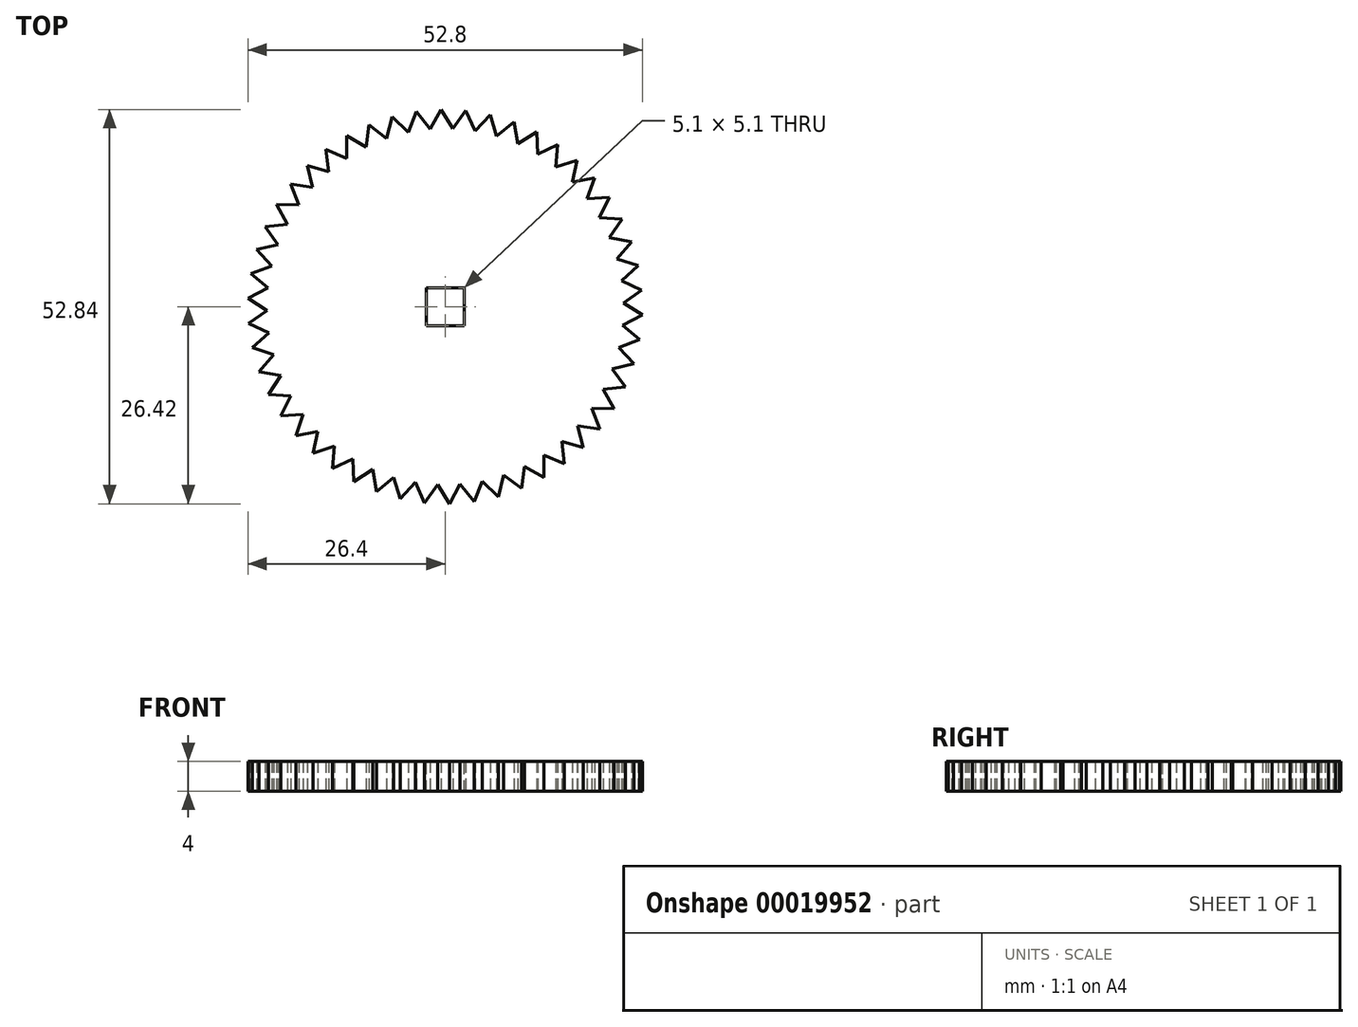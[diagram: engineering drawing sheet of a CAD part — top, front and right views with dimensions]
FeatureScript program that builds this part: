
annotation { "Feature Type Name" : "Feature", "Feature Type Description" : "" }
export const myFeature = defineFeature(function(context is Context, id is Id, definition is map)
    precondition{}
    {
        {
            var Q0;
            Q0=qCreatedBy(makeId("Top.planeOp"),FACE);
            var sketch = newSketch(context, id + "F0", { "sketchPlane" : qUnion([Q0])});
            skCircle(sketch, "E0.cCircle", {"center": v(0, 0) * mm, "radius": 23.83 * mm, "construction": true});
            skLineSegment(sketch, "E0.0", {"start": v(-2, 23.79) * mm, "end": v(1, 23.85) * mm});
            skLineSegment(sketch, "E0.1", {"start": v(1, 23.85) * mm, "end": v(3.98, 23.54) * mm});
            skLineSegment(sketch, "E0.2", {"start": v(3.98, 23.54) * mm, "end": v(6.9, 22.85) * mm});
            skLineSegment(sketch, "E0.3", {"start": v(6.9, 22.85) * mm, "end": v(9.71, 21.8) * mm});
            skLineSegment(sketch, "E0.4", {"start": v(9.71, 21.8) * mm, "end": v(12.37, 20.42) * mm});
            skLineSegment(sketch, "E0.5", {"start": v(12.37, 20.42) * mm, "end": v(14.83, 18.7) * mm});
            skLineSegment(sketch, "E0.6", {"start": v(14.83, 18.7) * mm, "end": v(17.06, 16.7) * mm});
            skLineSegment(sketch, "E0.7", {"start": v(17.06, 16.7) * mm, "end": v(19.02, 14.43) * mm});
            skLineSegment(sketch, "E0.8", {"start": v(19.02, 14.43) * mm, "end": v(20.67, 11.94) * mm});
            skLineSegment(sketch, "E0.9", {"start": v(20.67, 11.94) * mm, "end": v(22, 9.25) * mm});
            skLineSegment(sketch, "E0.10", {"start": v(22, 9.25) * mm, "end": v(23, 6.42) * mm});
            skLineSegment(sketch, "E0.11", {"start": v(23, 6.42) * mm, "end": v(23.62, 3.49) * mm});
            skLineSegment(sketch, "E0.12", {"start": v(23.62, 3.49) * mm, "end": v(23.87, 0.5) * mm});
            skLineSegment(sketch, "E0.13", {"start": v(23.87, 0.5) * mm, "end": v(23.74, -2.5) * mm});
            skLineSegment(sketch, "E0.14", {"start": v(23.74, -2.5) * mm, "end": v(23.24, -5.45) * mm});
            skLineSegment(sketch, "E0.15", {"start": v(23.24, -5.45) * mm, "end": v(22.38, -8.32) * mm});
            skLineSegment(sketch, "E0.16", {"start": v(22.38, -8.32) * mm, "end": v(21.16, -11.06) * mm});
            skLineSegment(sketch, "E0.17", {"start": v(21.16, -11.06) * mm, "end": v(19.6, -13.62) * mm});
            skLineSegment(sketch, "E0.18", {"start": v(19.6, -13.62) * mm, "end": v(17.74, -15.97) * mm});
            skLineSegment(sketch, "E0.19", {"start": v(17.74, -15.97) * mm, "end": v(15.6, -18.07) * mm});
            skLineSegment(sketch, "E0.20", {"start": v(15.6, -18.07) * mm, "end": v(13.21, -19.88) * mm});
            skLineSegment(sketch, "E0.21", {"start": v(13.21, -19.88) * mm, "end": v(10.61, -21.38) * mm});
            skLineSegment(sketch, "E0.22", {"start": v(10.61, -21.38) * mm, "end": v(7.85, -22.55) * mm});
            skLineSegment(sketch, "E0.23", {"start": v(7.85, -22.55) * mm, "end": v(4.96, -23.35) * mm});
            skLineSegment(sketch, "E0.24", {"start": v(4.96, -23.35) * mm, "end": v(2, -23.79) * mm});
            skLineSegment(sketch, "E0.25", {"start": v(2, -23.79) * mm, "end": v(-1, -23.85) * mm});
            skLineSegment(sketch, "E0.26", {"start": v(-1, -23.85) * mm, "end": v(-3.98, -23.54) * mm});
            skLineSegment(sketch, "E0.27", {"start": v(-3.98, -23.54) * mm, "end": v(-6.9, -22.85) * mm});
            skLineSegment(sketch, "E0.28", {"start": v(-6.9, -22.85) * mm, "end": v(-9.71, -21.8) * mm});
            skLineSegment(sketch, "E0.29", {"start": v(-9.71, -21.8) * mm, "end": v(-12.37, -20.42) * mm});
            skLineSegment(sketch, "E0.30", {"start": v(-12.37, -20.42) * mm, "end": v(-14.83, -18.7) * mm});
            skLineSegment(sketch, "E0.31", {"start": v(-14.83, -18.7) * mm, "end": v(-17.06, -16.7) * mm});
            skLineSegment(sketch, "E0.32", {"start": v(-17.06, -16.7) * mm, "end": v(-19.02, -14.43) * mm});
            skLineSegment(sketch, "E0.33", {"start": v(-19.02, -14.43) * mm, "end": v(-20.67, -11.94) * mm});
            skLineSegment(sketch, "E0.34", {"start": v(-20.67, -11.94) * mm, "end": v(-22, -9.25) * mm});
            skLineSegment(sketch, "E0.35", {"start": v(-22, -9.25) * mm, "end": v(-23, -6.42) * mm});
            skLineSegment(sketch, "E0.36", {"start": v(-23, -6.42) * mm, "end": v(-23.62, -3.49) * mm});
            skLineSegment(sketch, "E0.37", {"start": v(-23.62, -3.49) * mm, "end": v(-23.87, -0.5) * mm});
            skLineSegment(sketch, "E0.38", {"start": v(-23.87, -0.5) * mm, "end": v(-23.74, 2.5) * mm});
            skLineSegment(sketch, "E0.39", {"start": v(-23.74, 2.5) * mm, "end": v(-23.24, 5.45) * mm});
            skLineSegment(sketch, "E0.40", {"start": v(-23.24, 5.45) * mm, "end": v(-22.38, 8.32) * mm});
            skLineSegment(sketch, "E0.41", {"start": v(-22.38, 8.32) * mm, "end": v(-21.16, 11.06) * mm});
            skLineSegment(sketch, "E0.42", {"start": v(-21.16, 11.06) * mm, "end": v(-19.6, 13.62) * mm});
            skLineSegment(sketch, "E0.43", {"start": v(-19.6, 13.62) * mm, "end": v(-17.74, 15.97) * mm});
            skLineSegment(sketch, "E0.44", {"start": v(-17.74, 15.97) * mm, "end": v(-15.6, 18.07) * mm});
            skLineSegment(sketch, "E0.45", {"start": v(-15.6, 18.07) * mm, "end": v(-13.21, 19.88) * mm});
            skLineSegment(sketch, "E0.46", {"start": v(-13.21, 19.88) * mm, "end": v(-10.61, 21.38) * mm});
            skLineSegment(sketch, "E0.47", {"start": v(-10.61, 21.38) * mm, "end": v(-7.85, 22.55) * mm});
            skLineSegment(sketch, "E0.48", {"start": v(-7.85, 22.55) * mm, "end": v(-4.96, 23.35) * mm});
            skLineSegment(sketch, "E0.49", {"start": v(-4.96, 23.35) * mm, "end": v(-2, 23.79) * mm});
            skPoint(sketch, "E0.0.midPoint", {"position": v(-0.5, 23.82) * mm});
            skLineSegment(sketch, "E1", {"start": v(-13.21, 19.88) * mm, "end": v(-13.21, 22.88) * mm});
            skLineSegment(sketch, "E2", {"start": v(-13.21, 22.88) * mm, "end": v(-10.61, 21.38) * mm});
            skLineSegment(sketch, "E3", {"start": v(-10.61, 21.38) * mm, "end": v(-10.24, 24.36) * mm});
            skLineSegment(sketch, "E4", {"start": v(-10.24, 24.36) * mm, "end": v(-7.85, 22.55) * mm});
            skLineSegment(sketch, "E5", {"start": v(-7.1, 25.45) * mm, "end": v(-4.96, 23.35) * mm});
            skLineSegment(sketch, "E6", {"start": v(-4.96, 23.35) * mm, "end": v(-3.86, 26.14) * mm});
            skLineSegment(sketch, "E7", {"start": v(-3.86, 26.14) * mm, "end": v(-2, 23.79) * mm});
            skLineSegment(sketch, "E8", {"start": v(-2, 23.79) * mm, "end": v(-0.55, 26.42) * mm});
            skLineSegment(sketch, "E9", {"start": v(-0.55, 26.42) * mm, "end": v(1, 23.85) * mm});
            skLineSegment(sketch, "E10", {"start": v(1, 23.85) * mm, "end": v(2.76, 26.28) * mm});
            skLineSegment(sketch, "E11", {"start": v(2.76, 26.28) * mm, "end": v(3.98, 23.54) * mm});
            skLineSegment(sketch, "E12", {"start": v(3.98, 23.54) * mm, "end": v(6.03, 25.72) * mm});
            skLineSegment(sketch, "E13", {"start": v(6.03, 25.72) * mm, "end": v(6.9, 22.85) * mm});
            skLineSegment(sketch, "E14", {"start": v(6.9, 22.85) * mm, "end": v(9.21, 24.77) * mm});
            skLineSegment(sketch, "E15", {"start": v(9.21, 24.77) * mm, "end": v(9.71, 21.8) * mm});
            skLineSegment(sketch, "E16", {"start": v(9.71, 21.8) * mm, "end": v(12.24, 23.42) * mm});
            skLineSegment(sketch, "E17", {"start": v(12.24, 23.42) * mm, "end": v(12.37, 20.42) * mm});
            skLineSegment(sketch, "E18", {"start": v(12.37, 20.42) * mm, "end": v(15.08, 21.7) * mm});
            skLineSegment(sketch, "E19", {"start": v(15.08, 21.7) * mm, "end": v(14.83, 18.7) * mm});
            skLineSegment(sketch, "E20", {"start": v(14.83, 18.7) * mm, "end": v(17.68, 19.64) * mm});
            skLineSegment(sketch, "E21", {"start": v(17.68, 19.64) * mm, "end": v(17.06, 16.7) * mm});
            skLineSegment(sketch, "E22", {"start": v(17.06, 16.7) * mm, "end": v(20, 17.26) * mm});
            skLineSegment(sketch, "E23", {"start": v(20, 17.26) * mm, "end": v(19.02, 14.43) * mm});
            skLineSegment(sketch, "E24", {"start": v(19.02, 14.43) * mm, "end": v(22, 14.62) * mm});
            skLineSegment(sketch, "E25", {"start": v(22, 14.62) * mm, "end": v(20.67, 11.94) * mm});
            skLineSegment(sketch, "E26", {"start": v(20.67, 11.94) * mm, "end": v(23.67, 11.75) * mm});
            skLineSegment(sketch, "E27", {"start": v(23.67, 11.75) * mm, "end": v(22, 9.25) * mm});
            skLineSegment(sketch, "E28", {"start": v(22, 9.25) * mm, "end": v(24.95, 8.69) * mm});
            skLineSegment(sketch, "E29", {"start": v(24.95, 8.69) * mm, "end": v(23, 6.42) * mm});
            skLineSegment(sketch, "E30", {"start": v(23, 6.42) * mm, "end": v(25.84, 5.5) * mm});
            skLineSegment(sketch, "E31", {"start": v(25.84, 5.5) * mm, "end": v(23.62, 3.49) * mm});
            skLineSegment(sketch, "E32", {"start": v(23.62, 3.49) * mm, "end": v(26.33, 2.21) * mm});
            skLineSegment(sketch, "E33", {"start": v(26.33, 2.21) * mm, "end": v(23.87, 0.5) * mm});
            skLineSegment(sketch, "E34", {"start": v(23.87, 0.5) * mm, "end": v(26.4, -1.1) * mm});
            skLineSegment(sketch, "E35", {"start": v(26.4, -1.1) * mm, "end": v(23.74, -2.5) * mm});
            skLineSegment(sketch, "E36", {"start": v(23.74, -2.5) * mm, "end": v(26.05, -4.4) * mm});
            skLineSegment(sketch, "E37", {"start": v(26.05, -4.4) * mm, "end": v(23.24, -5.45) * mm});
            skLineSegment(sketch, "E38", {"start": v(23.24, -5.45) * mm, "end": v(25.3, -7.64) * mm});
            skLineSegment(sketch, "E39", {"start": v(25.3, -7.64) * mm, "end": v(22.38, -8.32) * mm});
            skLineSegment(sketch, "E40", {"start": v(22.38, -8.32) * mm, "end": v(24.14, -10.75) * mm});
            skLineSegment(sketch, "E41", {"start": v(24.14, -10.75) * mm, "end": v(21.16, -11.06) * mm});
            skLineSegment(sketch, "E42", {"start": v(19.6, -13.62) * mm, "end": v(22.6, -13.69) * mm});
            skLineSegment(sketch, "E43", {"start": v(22.6, -13.69) * mm, "end": v(21.16, -11.06) * mm});
            skLineSegment(sketch, "E44", {"start": v(19.6, -13.62) * mm, "end": v(20.7, -16.41) * mm});
            skLineSegment(sketch, "E45", {"start": v(20.7, -16.41) * mm, "end": v(17.74, -15.97) * mm});
            skLineSegment(sketch, "E46", {"start": v(17.74, -15.97) * mm, "end": v(18.49, -18.88) * mm});
            skLineSegment(sketch, "E47", {"start": v(18.49, -18.88) * mm, "end": v(15.6, -18.07) * mm});
            skLineSegment(sketch, "E48", {"start": v(15.6, -18.07) * mm, "end": v(15.97, -21.05) * mm});
            skLineSegment(sketch, "E49", {"start": v(15.97, -21.05) * mm, "end": v(13.21, -19.88) * mm});
            skLineSegment(sketch, "E50", {"start": v(13.21, -19.88) * mm, "end": v(13.21, -22.88) * mm});
            skLineSegment(sketch, "E51", {"start": v(13.21, -22.88) * mm, "end": v(10.61, -21.38) * mm});
            skLineSegment(sketch, "E52", {"start": v(10.61, -21.38) * mm, "end": v(10.24, -24.36) * mm});
            skLineSegment(sketch, "E53", {"start": v(10.24, -24.36) * mm, "end": v(7.85, -22.55) * mm});
            skLineSegment(sketch, "E54", {"start": v(7.85, -22.55) * mm, "end": v(7.1, -25.45) * mm});
            skLineSegment(sketch, "E55", {"start": v(7.1, -25.45) * mm, "end": v(4.96, -23.35) * mm});
            skLineSegment(sketch, "E56", {"start": v(4.96, -23.35) * mm, "end": v(3.86, -26.14) * mm});
            skLineSegment(sketch, "E57", {"start": v(3.86, -26.14) * mm, "end": v(2, -23.79) * mm});
            skLineSegment(sketch, "E58", {"start": v(2, -23.79) * mm, "end": v(0.55, -26.42) * mm});
            skLineSegment(sketch, "E59", {"start": v(0.55, -26.42) * mm, "end": v(-1, -23.85) * mm});
            skLineSegment(sketch, "E60", {"start": v(-1, -23.85) * mm, "end": v(-2.76, -26.28) * mm});
            skLineSegment(sketch, "E61", {"start": v(-2.76, -26.28) * mm, "end": v(-3.98, -23.54) * mm});
            skLineSegment(sketch, "E62", {"start": v(-3.98, -23.54) * mm, "end": v(-6.03, -25.72) * mm});
            skLineSegment(sketch, "E63", {"start": v(-6.03, -25.72) * mm, "end": v(-6.9, -22.85) * mm});
            skLineSegment(sketch, "E64", {"start": v(-6.9, -22.85) * mm, "end": v(-9.21, -24.77) * mm});
            skLineSegment(sketch, "E65", {"start": v(-9.21, -24.77) * mm, "end": v(-9.71, -21.8) * mm});
            skLineSegment(sketch, "E66", {"start": v(-9.71, -21.8) * mm, "end": v(-12.24, -23.42) * mm});
            skLineSegment(sketch, "E67", {"start": v(-12.24, -23.42) * mm, "end": v(-12.37, -20.42) * mm});
            skLineSegment(sketch, "E68", {"start": v(-12.37, -20.42) * mm, "end": v(-15.08, -21.7) * mm});
            skLineSegment(sketch, "E69", {"start": v(-15.08, -21.7) * mm, "end": v(-14.83, -18.7) * mm});
            skLineSegment(sketch, "E70", {"start": v(-14.83, -18.7) * mm, "end": v(-17.68, -19.64) * mm});
            skLineSegment(sketch, "E71", {"start": v(-17.68, -19.64) * mm, "end": v(-17.06, -16.7) * mm});
            skLineSegment(sketch, "E72", {"start": v(-17.06, -16.7) * mm, "end": v(-20, -17.26) * mm});
            skLineSegment(sketch, "E73", {"start": v(-20, -17.26) * mm, "end": v(-19.02, -14.43) * mm});
            skLineSegment(sketch, "E74", {"start": v(-19.02, -14.43) * mm, "end": v(-22, -14.62) * mm});
            skLineSegment(sketch, "E75", {"start": v(-22, -14.62) * mm, "end": v(-20.67, -11.94) * mm});
            skLineSegment(sketch, "E76", {"start": v(-20.67, -11.94) * mm, "end": v(-23.67, -11.75) * mm});
            skLineSegment(sketch, "E77", {"start": v(-23.67, -11.75) * mm, "end": v(-22, -9.25) * mm});
            skLineSegment(sketch, "E78", {"start": v(-22, -9.25) * mm, "end": v(-24.95, -8.69) * mm});
            skLineSegment(sketch, "E79", {"start": v(-24.95, -8.69) * mm, "end": v(-23, -6.42) * mm});
            skLineSegment(sketch, "E80", {"start": v(-23, -6.42) * mm, "end": v(-25.84, -5.5) * mm});
            skLineSegment(sketch, "E81", {"start": v(-25.84, -5.5) * mm, "end": v(-23.62, -3.49) * mm});
            skLineSegment(sketch, "E82", {"start": v(-23.74, 2.5) * mm, "end": v(-26.05, 4.4) * mm});
            skLineSegment(sketch, "E83", {"start": v(-26.05, 4.4) * mm, "end": v(-23.24, 5.45) * mm});
            skLineSegment(sketch, "E84", {"start": v(-23.24, 5.45) * mm, "end": v(-25.3, 7.64) * mm});
            skLineSegment(sketch, "E85", {"start": v(-25.3, 7.64) * mm, "end": v(-22.38, 8.32) * mm});
            skLineSegment(sketch, "E86", {"start": v(-22.38, 8.32) * mm, "end": v(-24.14, 10.75) * mm});
            skLineSegment(sketch, "E87", {"start": v(-24.14, 10.75) * mm, "end": v(-21.16, 11.06) * mm});
            skLineSegment(sketch, "E88", {"start": v(-21.16, 11.06) * mm, "end": v(-22.6, 13.69) * mm});
            skLineSegment(sketch, "E89", {"start": v(-22.6, 13.69) * mm, "end": v(-19.6, 13.62) * mm});
            skLineSegment(sketch, "E90", {"start": v(-19.6, 13.62) * mm, "end": v(-20.7, 16.41) * mm});
            skLineSegment(sketch, "E91", {"start": v(-20.7, 16.41) * mm, "end": v(-17.74, 15.97) * mm});
            skLineSegment(sketch, "E92", {"start": v(-17.74, 15.97) * mm, "end": v(-18.49, 18.88) * mm});
            skLineSegment(sketch, "E93", {"start": v(-18.49, 18.88) * mm, "end": v(-15.6, 18.07) * mm});
            skLineSegment(sketch, "E94", {"start": v(-7.85, 22.55) * mm, "end": v(-7.1, 25.45) * mm});
            skLineSegment(sketch, "E95", {"start": v(-23.87, -0.5) * mm, "end": v(-26.4, 1.1) * mm});
            skLineSegment(sketch, "E96", {"start": v(-26.4, 1.1) * mm, "end": v(-23.74, 2.5) * mm});
            skLineSegment(sketch, "E97", {"start": v(-23.62, -3.49) * mm, "end": v(-26.33, -2.21) * mm});
            skLineSegment(sketch, "E98", {"start": v(-26.33, -2.21) * mm, "end": v(-23.87, -0.5) * mm});
            skLineSegment(sketch, "E99", {"start": v(-15.6, 18.07) * mm, "end": v(-15.97, 21.05) * mm});
            skLineSegment(sketch, "E100", {"start": v(-15.97, 21.05) * mm, "end": v(-13.21, 19.88) * mm});
            skSolve(sketch);
        }
        {
            var Q0;
            Q0=makeQuery(id+"F0.imprint","IMPRINT",FACE,{"disambiguationData":[TD([[makeQuery(id+"F0.imprint","IMPRINT",EDGE,{"derivedFrom":sQuery(id+"F0.wireOp",EDGE,"E0.0")}),1.0]])]});
            var Q1;
            Q1=makeQuery(id+"F0.imprint","IMPRINT",FACE,{"disambiguationData":[TD([[makeQuery(id+"F0.imprint","IMPRINT",EDGE,{"derivedFrom":sQuery(id+"F0.wireOp",EDGE,"E0.31")}),1.0]])]});
            var Q2;
            Q2=makeQuery(id+"F0.imprint","IMPRINT",FACE,{"disambiguationData":[TD([[makeQuery(id+"F0.imprint","IMPRINT",EDGE,{"derivedFrom":sQuery(id+"F0.wireOp",EDGE,"E0.1")}),1.0]])]});
            var Q3;
            Q3=makeQuery(id+"F0.imprint","IMPRINT",FACE,{"disambiguationData":[TD([[makeQuery(id+"F0.imprint","IMPRINT",EDGE,{"derivedFrom":sQuery(id+"F0.wireOp",EDGE,"E0.3")}),1.0]])]});
            var Q4;
            Q4=makeQuery(id+"F0.imprint","IMPRINT",FACE,{"disambiguationData":[TD([[makeQuery(id+"F0.imprint","IMPRINT",EDGE,{"derivedFrom":sQuery(id+"F0.wireOp",EDGE,"E0.49")}),1.0]])]});
            var Q5;
            Q5=makeQuery(id+"F0.imprint","IMPRINT",FACE,{"disambiguationData":[TD([[makeQuery(id+"F0.imprint","IMPRINT",EDGE,{"derivedFrom":sQuery(id+"F0.wireOp",EDGE,"E0.36")}),1.0]])]});
            var Q6;
            Q6=makeQuery(id+"F0.imprint","IMPRINT",FACE,{"disambiguationData":[TD([[makeQuery(id+"F0.imprint","IMPRINT",EDGE,{"derivedFrom":sQuery(id+"F0.wireOp",EDGE,"E0.44")}),1.0]])]});
            var Q7;
            Q7=makeQuery(id+"F0.imprint","IMPRINT",FACE,{"disambiguationData":[TD([[makeQuery(id+"F0.imprint","IMPRINT",EDGE,{"derivedFrom":sQuery(id+"F0.wireOp",EDGE,"E0.28")}),1.0]])]});
            var Q8;
            Q8=makeQuery(id+"F0.imprint","IMPRINT",FACE,{"disambiguationData":[TD([[makeQuery(id+"F0.imprint","IMPRINT",EDGE,{"derivedFrom":sQuery(id+"F0.wireOp",EDGE,"E0.21")}),1.0]])]});
            var Q9;
            Q9=makeQuery(id+"F0.imprint","IMPRINT",FACE,{"disambiguationData":[TD([[makeQuery(id+"F0.imprint","IMPRINT",EDGE,{"derivedFrom":sQuery(id+"F0.wireOp",EDGE,"E0.23")}),1.0]])]});
            var Q10;
            Q10=makeQuery(id+"F0.imprint","IMPRINT",FACE,{"disambiguationData":[TD([[makeQuery(id+"F0.imprint","IMPRINT",EDGE,{"derivedFrom":sQuery(id+"F0.wireOp",EDGE,"E0.39")}),1.0]])]});
            var Q11;
            Q11=makeQuery(id+"F0.imprint","IMPRINT",FACE,{"disambiguationData":[TD([[makeQuery(id+"F0.imprint","IMPRINT",EDGE,{"derivedFrom":sQuery(id+"F0.wireOp",EDGE,"E0.37")}),1.0]])]});
            var Q12;
            Q12=makeQuery(id+"F0.imprint","IMPRINT",FACE,{"disambiguationData":[TD([[makeQuery(id+"F0.imprint","IMPRINT",EDGE,{"derivedFrom":sQuery(id+"F0.wireOp",EDGE,"E0.47")}),1.0]])]});
            var Q13;
            Q13=makeQuery(id+"F0.imprint","IMPRINT",FACE,{"disambiguationData":[TD([[makeQuery(id+"F0.imprint","IMPRINT",EDGE,{"derivedFrom":sQuery(id+"F0.wireOp",EDGE,"E0.2")}),1.0]])]});
            var Q14;
            Q14=makeQuery(id+"F0.imprint","IMPRINT",FACE,{"disambiguationData":[TD([[makeQuery(id+"F0.imprint","IMPRINT",EDGE,{"derivedFrom":sQuery(id+"F0.wireOp",EDGE,"E0.20")}),1.0]])]});
            var Q15;
            Q15=makeQuery(id+"F0.imprint","IMPRINT",FACE,{"disambiguationData":[TD([[makeQuery(id+"F0.imprint","IMPRINT",EDGE,{"derivedFrom":sQuery(id+"F0.wireOp",EDGE,"E0.13")}),1.0]])]});
            var Q16;
            Q16=makeQuery(id+"F0.imprint","IMPRINT",FACE,{"disambiguationData":[TD([[makeQuery(id+"F0.imprint","IMPRINT",EDGE,{"derivedFrom":sQuery(id+"F0.wireOp",EDGE,"E0.17")}),1.0]])]});
            var Q17;
            Q17=makeQuery(id+"F0.imprint","IMPRINT",FACE,{"disambiguationData":[TD([[makeQuery(id+"F0.imprint","IMPRINT",EDGE,{"derivedFrom":sQuery(id+"F0.wireOp",EDGE,"E0.33")}),1.0]])]});
            var Q18;
            Q18=makeQuery(id+"F0.imprint","IMPRINT",FACE,{"disambiguationData":[TD([[makeQuery(id+"F0.imprint","IMPRINT",EDGE,{"derivedFrom":sQuery(id+"F0.wireOp",EDGE,"E0.0")}),-1.0]])]});
            var Q19;
            Q19=makeQuery(id+"F0.imprint","IMPRINT",FACE,{"disambiguationData":[TD([[makeQuery(id+"F0.imprint","IMPRINT",EDGE,{"derivedFrom":sQuery(id+"F0.wireOp",EDGE,"E0.24")}),1.0]])]});
            var Q20;
            Q20=makeQuery(id+"F0.imprint","IMPRINT",FACE,{"disambiguationData":[TD([[makeQuery(id+"F0.imprint","IMPRINT",EDGE,{"derivedFrom":sQuery(id+"F0.wireOp",EDGE,"E0.40")}),1.0]])]});
            var Q21;
            Q21=makeQuery(id+"F0.imprint","IMPRINT",FACE,{"disambiguationData":[TD([[makeQuery(id+"F0.imprint","IMPRINT",EDGE,{"derivedFrom":sQuery(id+"F0.wireOp",EDGE,"E0.15")}),1.0]])]});
            var Q22;
            Q22=makeQuery(id+"F0.imprint","IMPRINT",FACE,{"disambiguationData":[TD([[makeQuery(id+"F0.imprint","IMPRINT",EDGE,{"derivedFrom":sQuery(id+"F0.wireOp",EDGE,"E0.29")}),1.0]])]});
            var Q23;
            Q23=makeQuery(id+"F0.imprint","IMPRINT",FACE,{"disambiguationData":[TD([[makeQuery(id+"F0.imprint","IMPRINT",EDGE,{"derivedFrom":sQuery(id+"F0.wireOp",EDGE,"E0.6")}),1.0]])]});
            var Q24;
            Q24=makeQuery(id+"F0.imprint","IMPRINT",FACE,{"disambiguationData":[TD([[makeQuery(id+"F0.imprint","IMPRINT",EDGE,{"derivedFrom":sQuery(id+"F0.wireOp",EDGE,"E0.22")}),1.0]])]});
            var Q25;
            Q25=makeQuery(id+"F0.imprint","IMPRINT",FACE,{"disambiguationData":[TD([[makeQuery(id+"F0.imprint","IMPRINT",EDGE,{"derivedFrom":sQuery(id+"F0.wireOp",EDGE,"E0.34")}),1.0]])]});
            var Q26;
            Q26=makeQuery(id+"F0.imprint","IMPRINT",FACE,{"disambiguationData":[TD([[makeQuery(id+"F0.imprint","IMPRINT",EDGE,{"derivedFrom":sQuery(id+"F0.wireOp",EDGE,"E0.18")}),1.0]])]});
            var Q27;
            Q27=makeQuery(id+"F0.imprint","IMPRINT",FACE,{"disambiguationData":[TD([[makeQuery(id+"F0.imprint","IMPRINT",EDGE,{"derivedFrom":sQuery(id+"F0.wireOp",EDGE,"E0.38")}),1.0]])]});
            var Q28;
            Q28=makeQuery(id+"F0.imprint","IMPRINT",FACE,{"disambiguationData":[TD([[makeQuery(id+"F0.imprint","IMPRINT",EDGE,{"derivedFrom":sQuery(id+"F0.wireOp",EDGE,"E0.45")}),1.0]])]});
            var Q29;
            Q29=makeQuery(id+"F0.imprint","IMPRINT",FACE,{"disambiguationData":[TD([[makeQuery(id+"F0.imprint","IMPRINT",EDGE,{"derivedFrom":sQuery(id+"F0.wireOp",EDGE,"E0.14")}),1.0]])]});
            var Q30;
            Q30=makeQuery(id+"F0.imprint","IMPRINT",FACE,{"disambiguationData":[TD([[makeQuery(id+"F0.imprint","IMPRINT",EDGE,{"derivedFrom":sQuery(id+"F0.wireOp",EDGE,"E0.5")}),1.0]])]});
            var Q31;
            Q31=makeQuery(id+"F0.imprint","IMPRINT",FACE,{"disambiguationData":[TD([[makeQuery(id+"F0.imprint","IMPRINT",EDGE,{"derivedFrom":sQuery(id+"F0.wireOp",EDGE,"E0.19")}),1.0]])]});
            var Q32;
            Q32=makeQuery(id+"F0.imprint","IMPRINT",FACE,{"disambiguationData":[TD([[makeQuery(id+"F0.imprint","IMPRINT",EDGE,{"derivedFrom":sQuery(id+"F0.wireOp",EDGE,"E0.16")}),1.0]])]});
            var Q33;
            Q33=makeQuery(id+"F0.imprint","IMPRINT",FACE,{"disambiguationData":[TD([[makeQuery(id+"F0.imprint","IMPRINT",EDGE,{"derivedFrom":sQuery(id+"F0.wireOp",EDGE,"E0.4")}),1.0]])]});
            var Q34;
            Q34=makeQuery(id+"F0.imprint","IMPRINT",FACE,{"disambiguationData":[TD([[makeQuery(id+"F0.imprint","IMPRINT",EDGE,{"derivedFrom":sQuery(id+"F0.wireOp",EDGE,"E0.35")}),1.0]])]});
            var Q35;
            Q35=makeQuery(id+"F0.imprint","IMPRINT",FACE,{"disambiguationData":[TD([[makeQuery(id+"F0.imprint","IMPRINT",EDGE,{"derivedFrom":sQuery(id+"F0.wireOp",EDGE,"E0.26")}),1.0]])]});
            var Q36;
            Q36=makeQuery(id+"F0.imprint","IMPRINT",FACE,{"disambiguationData":[TD([[makeQuery(id+"F0.imprint","IMPRINT",EDGE,{"derivedFrom":sQuery(id+"F0.wireOp",EDGE,"E0.42")}),1.0]])]});
            var Q37;
            Q37=makeQuery(id+"F0.imprint","IMPRINT",FACE,{"disambiguationData":[TD([[makeQuery(id+"F0.imprint","IMPRINT",EDGE,{"derivedFrom":sQuery(id+"F0.wireOp",EDGE,"E0.41")}),1.0]])]});
            var Q38;
            Q38=makeQuery(id+"F0.imprint","IMPRINT",FACE,{"disambiguationData":[TD([[makeQuery(id+"F0.imprint","IMPRINT",EDGE,{"derivedFrom":sQuery(id+"F0.wireOp",EDGE,"E0.25")}),1.0]])]});
            var Q39;
            Q39=makeQuery(id+"F0.imprint","IMPRINT",FACE,{"disambiguationData":[TD([[makeQuery(id+"F0.imprint","IMPRINT",EDGE,{"derivedFrom":sQuery(id+"F0.wireOp",EDGE,"E0.43")}),1.0]])]});
            var Q40;
            Q40=makeQuery(id+"F0.imprint","IMPRINT",FACE,{"disambiguationData":[TD([[makeQuery(id+"F0.imprint","IMPRINT",EDGE,{"derivedFrom":sQuery(id+"F0.wireOp",EDGE,"E0.27")}),1.0]])]});
            var Q41;
            Q41=makeQuery(id+"F0.imprint","IMPRINT",FACE,{"disambiguationData":[TD([[makeQuery(id+"F0.imprint","IMPRINT",EDGE,{"derivedFrom":sQuery(id+"F0.wireOp",EDGE,"E0.48")}),1.0]])]});
            var Q42;
            Q42=makeQuery(id+"F0.imprint","IMPRINT",FACE,{"disambiguationData":[TD([[makeQuery(id+"F0.imprint","IMPRINT",EDGE,{"derivedFrom":sQuery(id+"F0.wireOp",EDGE,"E0.32")}),1.0]])]});
            var Q43;
            Q43=makeQuery(id+"F0.imprint","IMPRINT",FACE,{"disambiguationData":[TD([[makeQuery(id+"F0.imprint","IMPRINT",EDGE,{"derivedFrom":sQuery(id+"F0.wireOp",EDGE,"E0.12")}),1.0]])]});
            var Q44;
            Q44=makeQuery(id+"F0.imprint","IMPRINT",FACE,{"disambiguationData":[TD([[makeQuery(id+"F0.imprint","IMPRINT",EDGE,{"derivedFrom":sQuery(id+"F0.wireOp",EDGE,"E0.11")}),1.0]])]});
            var Q45;
            Q45=makeQuery(id+"F0.imprint","IMPRINT",FACE,{"disambiguationData":[TD([[makeQuery(id+"F0.imprint","IMPRINT",EDGE,{"derivedFrom":sQuery(id+"F0.wireOp",EDGE,"E0.10")}),1.0]])]});
            var Q46;
            Q46=makeQuery(id+"F0.imprint","IMPRINT",FACE,{"disambiguationData":[TD([[makeQuery(id+"F0.imprint","IMPRINT",EDGE,{"derivedFrom":sQuery(id+"F0.wireOp",EDGE,"E0.9")}),1.0]])]});
            var Q47;
            Q47=makeQuery(id+"F0.imprint","IMPRINT",FACE,{"disambiguationData":[TD([[makeQuery(id+"F0.imprint","IMPRINT",EDGE,{"derivedFrom":sQuery(id+"F0.wireOp",EDGE,"E0.8")}),1.0]])]});
            var Q48;
            Q48=makeQuery(id+"F0.imprint","IMPRINT",FACE,{"disambiguationData":[TD([[makeQuery(id+"F0.imprint","IMPRINT",EDGE,{"derivedFrom":sQuery(id+"F0.wireOp",EDGE,"E0.7")}),1.0]])]});
            var Q49;
            Q49=makeQuery(id+"F0.imprint","IMPRINT",FACE,{"disambiguationData":[TD([[makeQuery(id+"F0.imprint","IMPRINT",EDGE,{"derivedFrom":sQuery(id+"F0.wireOp",EDGE,"E0.46")}),1.0]])]});
            var Q50;
            Q50=makeQuery(id+"F0.imprint","IMPRINT",FACE,{"disambiguationData":[TD([[makeQuery(id+"F0.imprint","IMPRINT",EDGE,{"derivedFrom":sQuery(id+"F0.wireOp",EDGE,"E0.30")}),1.0]])]});
            extrude(context, id + "F1", {"entities" : qUnion([Q0, Q1, Q2, Q3, Q4, Q5, Q6, Q7, Q8, Q9, Q10, Q11, Q12, Q13, Q14, Q15, Q16, Q17, Q18, Q19, Q20, Q21, Q22, Q23, Q24, Q25, Q26, Q27, Q28, Q29, Q30, Q31, Q32, Q33, Q34, Q35, Q36, Q37, Q38, Q39, Q40, Q41, Q42, Q43, Q44, Q45, Q46, Q47, Q48, Q49, Q50]), "depth" : 4 * mm});
        }
        {
            var Q0;
            Q0=makeQuery(id+"F1.opExtrude","CAP_FACE",FACE,{"disambiguationData":[OSD([sQuery(id+"F0.wireOp",EDGE,"E1"),sQuery(id+"F0.wireOp",EDGE,"E2"),sQuery(id+"F0.wireOp",EDGE,"E3"),sQuery(id+"F0.wireOp",EDGE,"E4"),sQuery(id+"F0.wireOp",EDGE,"E5"),sQuery(id+"F0.wireOp",EDGE,"E6"),sQuery(id+"F0.wireOp",EDGE,"E7"),sQuery(id+"F0.wireOp",EDGE,"E8"),sQuery(id+"F0.wireOp",EDGE,"E9"),sQuery(id+"F0.wireOp",EDGE,"E10"),sQuery(id+"F0.wireOp",EDGE,"E11"),sQuery(id+"F0.wireOp",EDGE,"E12"),sQuery(id+"F0.wireOp",EDGE,"E13"),sQuery(id+"F0.wireOp",EDGE,"E14"),sQuery(id+"F0.wireOp",EDGE,"E15"),sQuery(id+"F0.wireOp",EDGE,"E16"),sQuery(id+"F0.wireOp",EDGE,"E17"),sQuery(id+"F0.wireOp",EDGE,"E18"),sQuery(id+"F0.wireOp",EDGE,"E19"),sQuery(id+"F0.wireOp",EDGE,"E20"),sQuery(id+"F0.wireOp",EDGE,"E21"),sQuery(id+"F0.wireOp",EDGE,"E22"),sQuery(id+"F0.wireOp",EDGE,"E23"),sQuery(id+"F0.wireOp",EDGE,"E24"),sQuery(id+"F0.wireOp",EDGE,"E25"),sQuery(id+"F0.wireOp",EDGE,"E26"),sQuery(id+"F0.wireOp",EDGE,"E27"),sQuery(id+"F0.wireOp",EDGE,"E28"),sQuery(id+"F0.wireOp",EDGE,"E29"),sQuery(id+"F0.wireOp",EDGE,"E30"),sQuery(id+"F0.wireOp",EDGE,"E31"),sQuery(id+"F0.wireOp",EDGE,"E32"),sQuery(id+"F0.wireOp",EDGE,"E33"),sQuery(id+"F0.wireOp",EDGE,"E34"),sQuery(id+"F0.wireOp",EDGE,"E35"),sQuery(id+"F0.wireOp",EDGE,"E36"),sQuery(id+"F0.wireOp",EDGE,"E37"),sQuery(id+"F0.wireOp",EDGE,"E38"),sQuery(id+"F0.wireOp",EDGE,"E39"),sQuery(id+"F0.wireOp",EDGE,"E40"),sQuery(id+"F0.wireOp",EDGE,"E41"),sQuery(id+"F0.wireOp",EDGE,"E42"),sQuery(id+"F0.wireOp",EDGE,"E43"),sQuery(id+"F0.wireOp",EDGE,"E44"),sQuery(id+"F0.wireOp",EDGE,"E45"),sQuery(id+"F0.wireOp",EDGE,"E46"),sQuery(id+"F0.wireOp",EDGE,"E47"),sQuery(id+"F0.wireOp",EDGE,"E48"),sQuery(id+"F0.wireOp",EDGE,"E49"),sQuery(id+"F0.wireOp",EDGE,"E50"),sQuery(id+"F0.wireOp",EDGE,"E51"),sQuery(id+"F0.wireOp",EDGE,"E52"),sQuery(id+"F0.wireOp",EDGE,"E53"),sQuery(id+"F0.wireOp",EDGE,"E54"),sQuery(id+"F0.wireOp",EDGE,"E55"),sQuery(id+"F0.wireOp",EDGE,"E56"),sQuery(id+"F0.wireOp",EDGE,"E57"),sQuery(id+"F0.wireOp",EDGE,"E58"),sQuery(id+"F0.wireOp",EDGE,"E59"),sQuery(id+"F0.wireOp",EDGE,"E60"),sQuery(id+"F0.wireOp",EDGE,"E61"),sQuery(id+"F0.wireOp",EDGE,"E62"),sQuery(id+"F0.wireOp",EDGE,"E63"),sQuery(id+"F0.wireOp",EDGE,"E64"),sQuery(id+"F0.wireOp",EDGE,"E65"),sQuery(id+"F0.wireOp",EDGE,"E66"),sQuery(id+"F0.wireOp",EDGE,"E67"),sQuery(id+"F0.wireOp",EDGE,"E68"),sQuery(id+"F0.wireOp",EDGE,"E69"),sQuery(id+"F0.wireOp",EDGE,"E70"),sQuery(id+"F0.wireOp",EDGE,"E71"),sQuery(id+"F0.wireOp",EDGE,"E72"),sQuery(id+"F0.wireOp",EDGE,"E73"),sQuery(id+"F0.wireOp",EDGE,"E74"),sQuery(id+"F0.wireOp",EDGE,"E75"),sQuery(id+"F0.wireOp",EDGE,"E76"),sQuery(id+"F0.wireOp",EDGE,"E77"),sQuery(id+"F0.wireOp",EDGE,"E78"),sQuery(id+"F0.wireOp",EDGE,"E79"),sQuery(id+"F0.wireOp",EDGE,"E80"),sQuery(id+"F0.wireOp",EDGE,"E81"),sQuery(id+"F0.wireOp",EDGE,"E82"),sQuery(id+"F0.wireOp",EDGE,"E83"),sQuery(id+"F0.wireOp",EDGE,"E84"),sQuery(id+"F0.wireOp",EDGE,"E85"),sQuery(id+"F0.wireOp",EDGE,"E86"),sQuery(id+"F0.wireOp",EDGE,"E87"),sQuery(id+"F0.wireOp",EDGE,"E88"),sQuery(id+"F0.wireOp",EDGE,"E89"),sQuery(id+"F0.wireOp",EDGE,"E90"),sQuery(id+"F0.wireOp",EDGE,"E91"),sQuery(id+"F0.wireOp",EDGE,"E92"),sQuery(id+"F0.wireOp",EDGE,"E93"),sQuery(id+"F0.wireOp",EDGE,"E94"),sQuery(id+"F0.wireOp",EDGE,"E95"),sQuery(id+"F0.wireOp",EDGE,"E96"),sQuery(id+"F0.wireOp",EDGE,"E97"),sQuery(id+"F0.wireOp",EDGE,"E98"),sQuery(id+"F0.wireOp",EDGE,"E99"),sQuery(id+"F0.wireOp",EDGE,"E100")])],"isStart":false});
            var sketch = newSketch(context, id + "F2", { "sketchPlane" : qUnion([Q0])});
            skLineSegment(sketch, "E101.rect.bottom", {"start": v(2.55, 2.55) * mm, "end": v(-2.55, 2.55) * mm});
            skLineSegment(sketch, "E101.rect.top", {"start": v(2.55, -2.55) * mm, "end": v(-2.55, -2.55) * mm});
            skLineSegment(sketch, "E101.rect.left", {"start": v(2.55, 2.55) * mm, "end": v(2.55, -2.55) * mm});
            skLineSegment(sketch, "E101.rect.right", {"start": v(-2.55, 2.55) * mm, "end": v(-2.55, -2.55) * mm});
            skPoint(sketch, "E101.rect.middle", {"position": v(0, 0) * mm});
            skSolve(sketch);
        }
        {
            var Q0;
            Q0=makeQuery(id+"F2.imprint","IMPRINT",FACE,{"disambiguationData":[TD([[makeQuery(id+"F2.imprint","IMPRINT",EDGE,{"derivedFrom":sQuery(id+"F2.wireOp",EDGE,"E101.rect.bottom")}),1.0]])]});
            extrude(context, id + "F3", {"entities" : qUnion([Q0]), "operationType" : NewBodyOperationType.REMOVE, "oppositeDirection" : true, "depth" : 4 * mm});
        }
    });
